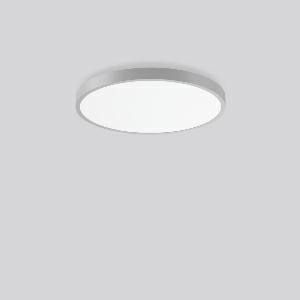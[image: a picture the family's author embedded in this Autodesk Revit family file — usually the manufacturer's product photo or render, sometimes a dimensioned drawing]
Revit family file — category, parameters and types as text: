
# Revit family: triona_round_a_312384_004_730_54a2
name_source: partatom
category: Lighting Fixtures
units: mm (PartAtom-declared; Revit-internal decimal feet)

## family parameters
Cut with Voids When Loaded = No
Host = Face
Light Source = No
Part Type = Normal
Room Calculation Point = No
Round Connector Dimension = Use Diameter
Shared = No

## types (1)
- TRIONA round A (1 x LED Modul 830, 9300 lm, 3000)
    Apparent Load = 106 VA
    CIE Flux Codes = 49 80 96 72 100
    Color Rendering = 80
    Color Temperature = 3000
    Default Elevation = 1800 mm
    Description = Series: TRIONA round
Decorative round LED surface-mounted luminaire. Flat, seamless frame: aluminium extrusion profile, powder coated. Cover made of sheet steel, powder-coated. Direct light emission through a diffuser plastic opal. Indirect light emission through a flush diffuser made of satin-finish plastic. Lightguide and diffuser made of non-yellowing plastic (PMMA). Lateral light emission (RZB SIDELITE technology) for above-average homogeneous light distribution. Direct 70%, indirect 30% light emission. Suitable for Ceiling mounting, Wall (surface). Tool-free mounting via bayonet connection. Electronic ballast included. Very easy installation thanks to Plug+Play connection. With Casambi smart+free Bluetooth control for wireless network and operation using Android / iOS devices, free app available for download. 
Colour: silver, matt (approx. RAL 9006)
Diameter: 681 mm
Height: 88 mm
Lamp: LED
Socket: without socket
Colour temperature: 3000K
Colour rendering index (CRI): 80
System power: 106 W
Rated luminous flux: 9300 lm
Luminous efficiency: 88 lm/W
Control gear: Dimmable Bluetooth converter
Protection class: I
Type of protection: IP 20
    Height = 88 mm
    Lamp = 1 x LED Modul 830
    Lamp Light Flux = 9300 lm
    Lamp count = 1
    Length = 681 mm
    Lifetime = 50000 h
    Luminous efficacy = 88 lm/W
    Manufacturer = RZB
    ModVariant = No
    Model = 312384.004.730
    Mounting Place = Ceiling
    Mounting Type = Surface mounted
    Number of Poles = 1
    OnlyDefault = Yes
    Power Factor = 1
    Product Name = TRIONA round A
    Product group = Surface mounted modular luminaires
    ProductGroupID = 306
    Protection Class = Protection class I
    Protection Degree = IP 20
    RLX_Detail_Level = 1
    RLX_Emergency_Light_Flux = 0 lm
    RLX_Emergency_Type = 0
    RLX_Emergency_Type_DB = No
    RlxData = <blob elided: 41681 chars, md5=d3e6752b>
    Socket = socket
    Standby Power = 0 W
    System Light Flux = 9300 lm
    System Power = 106 W
    Type Comments = Product without accessories
    Type Image = 312384.004.jpg
    URL = http://relux.com
    VarID = ---
    Voltage = 230 V
    Voltage Range = 220-240 V
    Weight = 0.00 kg
    Width = 0 mm  [stored 0 ft]

note: [stored X ft] marks values corroborated as IEEE doubles in the binary element streams (Revit-internal decimal feet)

## geometry (parser evidence)
native form markers: Blend x4, Sweep x11
no freeform markers — native parametric forms only
